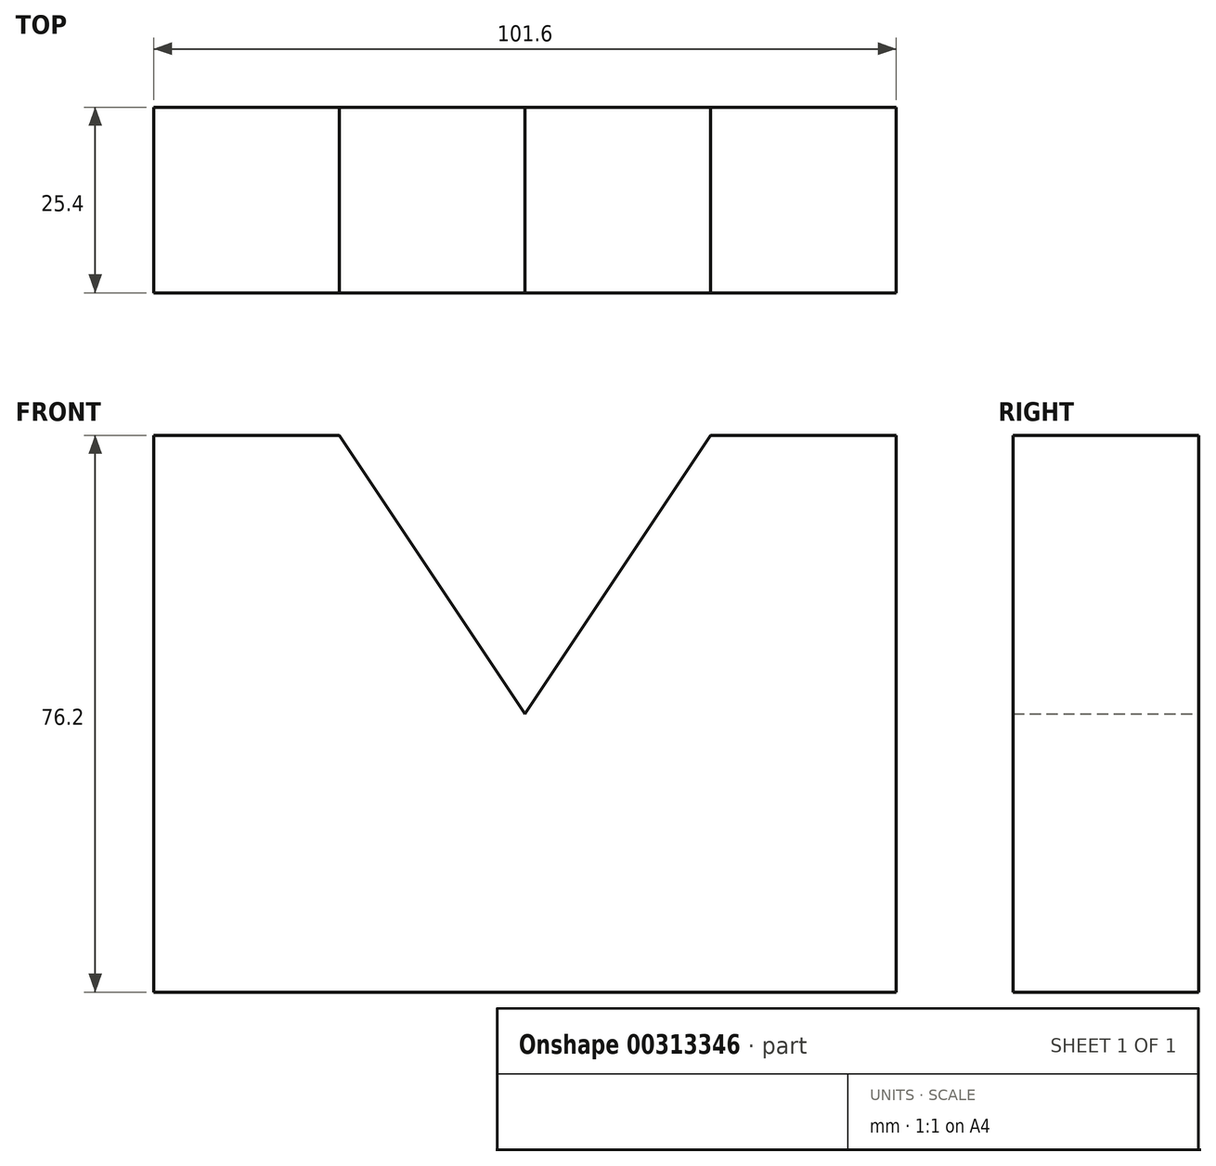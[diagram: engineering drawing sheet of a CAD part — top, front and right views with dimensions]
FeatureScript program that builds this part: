
annotation { "Feature Type Name" : "Feature", "Feature Type Description" : "" }
export const myFeature = defineFeature(function(context is Context, id is Id, definition is map)
    precondition{}
    {
        {
            var Q0;
            Q0=qCreatedBy(makeId("Front.planeOp"),FACE);
            var sketch = newSketch(context, id + "F0", { "sketchPlane" : qUnion([Q0])});
            skLineSegment(sketch, "E0", {"start": v(-46.84, -51.92) * mm, "end": v(54.76, -51.92) * mm});
            skLineSegment(sketch, "E1", {"start": v(-46.84, -51.92) * mm, "end": v(-46.84, 24.28) * mm});
            skLineSegment(sketch, "E2", {"start": v(-46.84, 24.28) * mm, "end": v(-21.44, 24.28) * mm});
            skLineSegment(sketch, "E3", {"start": v(54.76, -51.92) * mm, "end": v(54.76, 24.28) * mm});
            skLineSegment(sketch, "E4", {"start": v(54.76, 24.28) * mm, "end": v(29.36, 24.28) * mm});
            skLineSegment(sketch, "E5", {"start": v(3.96, -13.82) * mm, "end": v(29.36, 24.28) * mm});
            skPoint(sketch, "E5.startSnap0", {"position": v(3.96, -51.92) * mm});
            skLineSegment(sketch, "E6", {"start": v(3.96, -13.82) * mm, "end": v(-21.44, 24.28) * mm});
            skSolve(sketch);
        }
        {
            var Q0;
            Q0=makeQuery(id+"F0.imprint","IMPRINT",FACE,{"disambiguationData":[TD([[makeQuery(id+"F0.imprint","IMPRINT",EDGE,{"derivedFrom":sQuery(id+"F0.wireOp",EDGE,"E0")}),1.0]])]});
            extrude(context, id + "F1", {"entities" : qUnion([Q0]), "depth" : 25.4 * mm});
        }
    });
